FCSTD DOCUMENT  (FreeCAD 0.15R4671 (Git))
Label: ZTopBearingMount
License: All rights reserved
LicenseURL: http://en.wikipedia.org/wiki/All_rights_reserved
objects: Sketcher::SketchObject×6, PartDesign::Fillet×5, PartDesign::Pocket×4, Mesh::Feature×3, PartDesign::Pad×2, Part::Feature×1, PartDesign::Chamfer×1
note: 25 computed .brp shape members not serialized (recipe doc carries the construction recipe); baked Part::Feature solids carry a one-line shape summary decoded from their .brp

FEATURE [Mesh::Feature] HexNutStyle1_M
  Placement = pos=(-0.8,116,22) rot=(1,0,0;1.5708rad)
FEATURE [Mesh::Feature] HexNutStyle1_M001
  Placement = pos=(29.2,116,22) rot=(1,0,0;1.5708rad)
FEATURE [Part::Feature] Part__Feature  label="ZRodHolderTop"
  shape: bbox 156.7 x 36 x 15.66 mm, 185 faces (baked)
FEATURE [Sketcher::SketchObject] Sketch
  Placement = pos=(0,-5,0) rot=(-1,0,0;4.71239rad)
  sketch-geometry (8):
    g0: LineSegment StartX=22.25 StartY=7.5 StartZ=0 EndX=22.25 EndY=-27.5 EndZ=0
    g1: LineSegment StartX=22.25 StartY=-27.5 StartZ=0 EndX=-22.25 EndY=-27.5 EndZ=0
    g2: LineSegment StartX=-22.25 StartY=-27.5 StartZ=0 EndX=-22.25 EndY=7.5 EndZ=0
    g3: LineSegment StartX=22.25 StartY=7.5 StartZ=0 EndX=7.75 EndY=7.5 EndZ=0
    g4: LineSegment StartX=7.75 StartY=7.5 StartZ=0 EndX=7.75 EndY=-8 EndZ=0
    g5: LineSegment StartX=7.75 StartY=-8 StartZ=0 EndX=-7.75 EndY=-8 EndZ=0
    g6: LineSegment StartX=-7.75 StartY=-8 StartZ=0 EndX=-7.75 EndY=7.5 EndZ=0
    g7: LineSegment StartX=-7.75 StartY=7.5 StartZ=0 EndX=-22.25 EndY=7.5 EndZ=0
  constraints (23):
    c: Coincident(g0,g1)
    c: Coincident(g1,g2)
    c: Horizontal(g1)
    c: Vertical(g0)
    c: Vertical(g2)
    c: Horizontal(g3)
    c: Coincident(g3,g4)
    c: Vertical(g4)
    c: Coincident(g4,g5)
    c: Horizontal(g5)
    c: Coincident(g5,g6)
    c: Vertical(g6)
    c: Coincident(g6,g7)
    c: Coincident(g7,g2)
    c: Horizontal(g7)
    c: Coincident(g0,g3)
    c: DistanceX(g6) = -7.75
    c: DistanceY(g6) = 7.5
    c: DistanceY(g5) = -8
    c: DistanceX(g4) = 7.75
    c: DistanceY(g3) = 7.5
    c: DistanceX(g0) = 22.25
    c: DistanceY(g2,g1) = -35
FEATURE [PartDesign::Pad] Pad
  Length = 4
  Length2 = 100
  Placement = pos=(0,-5,0) rot=(-1,0,0;4.71239rad)
  Sketch = -> Sketch
  Type = 0
FEATURE [Mesh::Feature] _08ZZ_Ball_Bearing  label="608ZZ_Ball_Bearing"
  Placement = pos=(0,-28,-22) rot=(0,0,1;0rad)
FEATURE [Sketcher::SketchObject] Sketch001
  Placement = pos=(0,-9,0) rot=(1,0,0;1.5708rad)
  Support = -> Pad [Face10]
  sketch-geometry (4):
    g0: LineSegment StartX=22.25 StartY=-18.5 StartZ=0 EndX=-22.25 EndY=-18.5 EndZ=0
    g1: LineSegment StartX=-22.25 StartY=-18.5 StartZ=0 EndX=-22.25 EndY=-27.5 EndZ=0
    g2: LineSegment StartX=-22.25 StartY=-27.5 StartZ=0 EndX=22.25 EndY=-27.5 EndZ=0
    g3: LineSegment StartX=22.25 StartY=-27.5 StartZ=0 EndX=22.25 EndY=-18.5 EndZ=0
  constraints (8):
    c: Coincident(g0,g1)
    c: Coincident(g1,g2)
    c: Coincident(g2,g3)
    c: Coincident(g3,g0)
    c: Horizontal(g0)
    c: Horizontal(g2)
    c: Vertical(g1)
    c: Vertical(g3)
FEATURE [PartDesign::Pad] Pad001
  Length = 33
  Length2 = 100
  Placement = pos=(0,-5,0) rot=(-1,0,0;4.71239rad)
  Sketch = -> Sketch001
  Type = 0
FEATURE [PartDesign::Chamfer] Chamfer
  Base = -> Pad001 [Edge28,Edge26]
  Placement = pos=(0,-5,0) rot=(-1,0,0;4.71239rad)
  Size = 14
FEATURE [PartDesign::Fillet] Fillet
  Base = -> Chamfer [Edge7,Edge14,Edge21,Edge24]
  Placement = pos=(0,-5,0) rot=(-1,0,0;4.71239rad)
  Radius = 4
FEATURE [Sketcher::SketchObject] Sketch002
  Placement = pos=(0,-5,-18.5) rot=(0,0,1;3.14159rad)
  Support = -> Fillet [Face1]
  sketch-geometry (1):
    g0: Circle CenterX=0 CenterY=23 CenterZ=0 NormalX=0 NormalY=0 NormalZ=1 Radius=11.25
  constraints (2):
    c: PointOnObject(g0,g-2)
    c: Radius(g0) = 11.25
FEATURE [PartDesign::Pocket] Pocket
  Length = 7.5
  Placement = pos=(0,-5,0) rot=(-1,0,0;4.71239rad)
  Sketch = -> Sketch002
  Type = 0
FEATURE [Sketcher::SketchObject] Sketch003
  Placement = pos=(0,-5,-27.5) rot=(1,0,0;3.14159rad)
  Support = -> Pocket [Face13]
  sketch-geometry (1):
    g0: Circle CenterX=0 CenterY=23 CenterZ=0 NormalX=0 NormalY=0 NormalZ=1 Radius=9
  constraints (1):
    c: PointOnObject(g0,g-2)
FEATURE [PartDesign::Pocket] Pocket001
  Length = 5
  Placement = pos=(0,-5,0) rot=(-1,0,0;4.71239rad)
  Sketch = -> Sketch003
  Type = 1
FEATURE [Sketcher::SketchObject] Sketch004
  Placement = pos=(0,-9,0) rot=(1,0,0;1.5708rad)
  Support = -> Pocket001 [Face4]
  sketch-geometry (2):
    g0: Circle CenterX=-15 CenterY=0 CenterZ=0 NormalX=0 NormalY=0 NormalZ=1 Radius=1.8
    g1: Circle CenterX=15 CenterY=0 CenterZ=0 NormalX=0 NormalY=0 NormalZ=1 Radius=1.8
  constraints (4):
    c: PointOnObject(g0,g-1)
    c: PointOnObject(g1,g-1)
    c: Radius(g0) = 1.8
    c: Equal(g0,g1)
FEATURE [PartDesign::Pocket] Pocket002
  Length = 5
  Placement = pos=(0,-5,0) rot=(-1,0,0;4.71239rad)
  Sketch = -> Sketch004
  Type = 1
FEATURE [Sketcher::SketchObject] Sketch005
  Placement = pos=(0,-9,0) rot=(1,0,0;1.5708rad)
  Support = -> Pocket002 [Face4]
  sketch-geometry (2):
    g0: Circle CenterX=-15 CenterY=0 CenterZ=0 NormalX=0 NormalY=0 NormalZ=1 Radius=3.6
    g1: Circle CenterX=15 CenterY=0 CenterZ=0 NormalX=0 NormalY=0 NormalZ=1 Radius=3.6
  constraints (3):
    c: PointOnObject(g1,g-1)
    c: Radius(g1) = 3.6
    c: Equal(g1,g0)
FEATURE [PartDesign::Pocket] Pocket003
  Length = 2
  Placement = pos=(0,-5,0) rot=(-1,0,0;4.71239rad)
  Sketch = -> Sketch005
  Type = 0
FEATURE [PartDesign::Fillet] Fillet001
  Base = -> Pocket003 [Edge24,Edge20]
  Placement = pos=(0,-5,0) rot=(-1,0,0;4.71239rad)
  Radius = 3.5
FEATURE [PartDesign::Fillet] Fillet002
  Base = -> Fillet001 [Edge24]
  Placement = pos=(0,-5,0) rot=(-1,0,0;4.71239rad)
  Radius = 1
FEATURE [PartDesign::Fillet] Fillet003
  Base = -> Fillet002 [Edge22]
  Placement = pos=(0,-5,0) rot=(-1,0,0;4.71239rad)
  Radius = 1
FEATURE [PartDesign::Fillet] Fillet004  label="ZTopBearingMount"
  Base = -> Fillet003 [Edge75,Edge76,Edge44,Edge9]
  Placement = pos=(0,-5,0) rot=(-1,0,0;4.71239rad)
  Radius = 1
